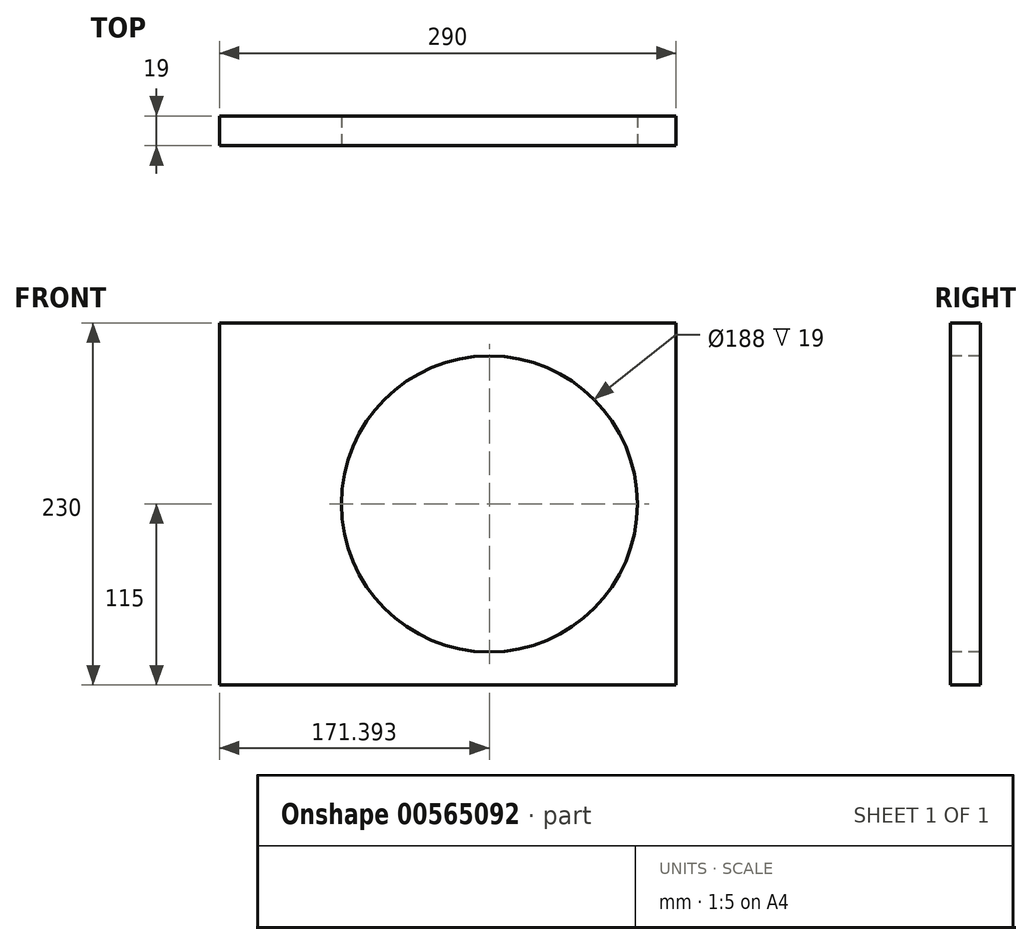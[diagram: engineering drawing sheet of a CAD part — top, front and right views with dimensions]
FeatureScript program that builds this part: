
annotation { "Feature Type Name" : "Feature", "Feature Type Description" : "" }
export const myFeature = defineFeature(function(context is Context, id is Id, definition is map)
    precondition{}
    {
        {
            var Q0;
            Q0=qCreatedBy(makeId("Front.planeOp"),FACE);
            var sketch = newSketch(context, id + "F0", { "sketchPlane" : qUnion([Q0])});
            skLineSegment(sketch, "E0.bottom", {"start": v(0, 0) * mm, "end": v(290, 0) * mm});
            skLineSegment(sketch, "E0.top", {"start": v(0, 230) * mm, "end": v(290, 230) * mm});
            skLineSegment(sketch, "E0.left", {"start": v(0, 0) * mm, "end": v(0, 230) * mm});
            skLineSegment(sketch, "E0.right", {"start": v(290, 0) * mm, "end": v(290, 230) * mm});
            skSolve(sketch);
        }
        {
            var Q0;
            Q0=makeQuery(id+"F0.imprint","IMPRINT",FACE,{"disambiguationData":[TD([[makeQuery(id+"F0.imprint","IMPRINT",EDGE,{"derivedFrom":sQuery(id+"F0.wireOp",EDGE,"E0.bottom")}),1.0]])]});
            extrude(context, id + "F1", {"entities" : qUnion([Q0]), "depth" : 19 * mm, "offsetDistance" : 25 * mm});
        }
        {
            var Q0;
            Q0=makeQuery(id+"F1.opExtrude","CAP_FACE",FACE,{"disambiguationData":[OSD([sQuery(id+"F0.wireOp",EDGE,"E0.bottom"),sQuery(id+"F0.wireOp",EDGE,"E0.top"),sQuery(id+"F0.wireOp",EDGE,"E0.left"),sQuery(id+"F0.wireOp",EDGE,"E0.right")])],"isStart":false});
            var sketch = newSketch(context, id + "F2", { "sketchPlane" : qUnion([Q0])});
            skCircle(sketch, "E1", {"center": v(171.4, 115) * mm, "radius": 94 * mm});
            skPoint(sketch, "E1.centerSnap0", {"position": v(290, 115) * mm});
            skSolve(sketch);
        }
        {
            var Q0;
            Q0=makeQuery(id+"F2.imprint","IMPRINT",FACE,{"disambiguationData":[TD([[makeQuery(id+"F2.imprint","IMPRINT",EDGE,{"derivedFrom":sQuery(id+"F2.wireOp",EDGE,"E1")}),1.0]])]});
            extrude(context, id + "F3", {"entities" : qUnion([Q0]), "operationType" : NewBodyOperationType.REMOVE, "oppositeDirection" : true, "depth" : 19 * mm, "offsetDistance" : 25 * mm});
        }
    });
